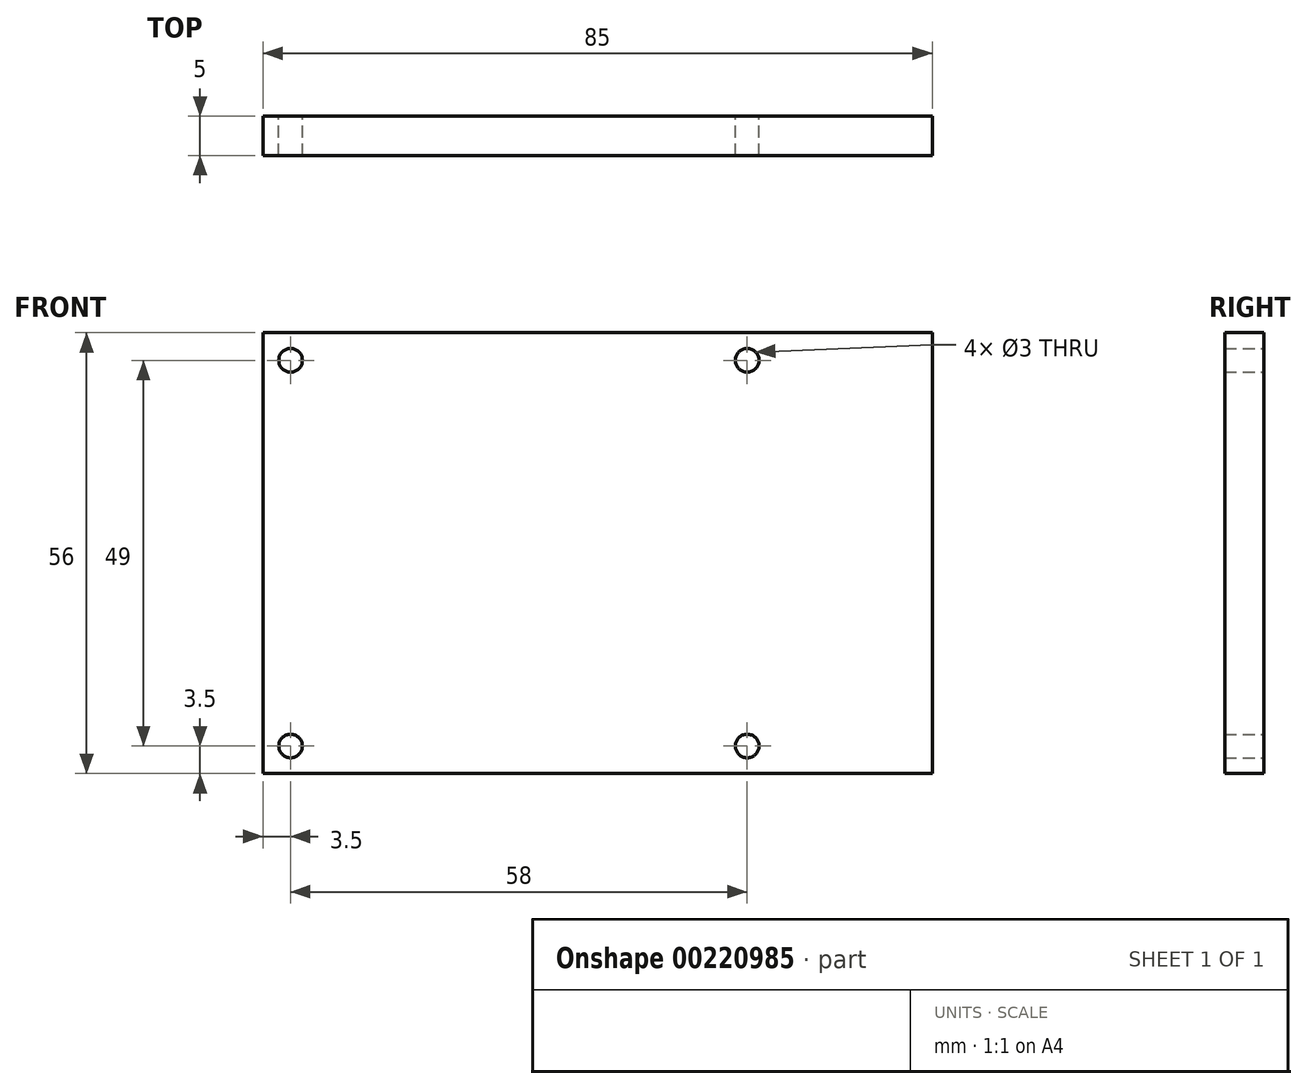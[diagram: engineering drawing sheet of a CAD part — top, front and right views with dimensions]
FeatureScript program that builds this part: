
annotation { "Feature Type Name" : "Feature", "Feature Type Description" : "" }
export const myFeature = defineFeature(function(context is Context, id is Id, definition is map)
    precondition{}
    {
        {
            var Q0;
            Q0=qCreatedBy(makeId("Front.planeOp"),FACE);
            var sketch = newSketch(context, id + "F0", { "sketchPlane" : qUnion([Q0])});
            skLineSegment(sketch, "E0.bottom", {"start": v(42.5, 28) * mm, "end": v(-42.5, 28) * mm});
            skLineSegment(sketch, "E0.top", {"start": v(42.5, -28) * mm, "end": v(-42.5, -28) * mm});
            skLineSegment(sketch, "E0.left", {"start": v(42.5, 28) * mm, "end": v(42.5, -28) * mm});
            skLineSegment(sketch, "E0.right", {"start": v(-42.5, 28) * mm, "end": v(-42.5, -28) * mm});
            skPoint(sketch, "E0.middle", {"position": v(0, 0) * mm});
            skLineSegment(sketch, "E1", {"start": v(-42.5, -28) * mm, "end": v(-39, -28) * mm});
            skLineSegment(sketch, "E2", {"start": v(-39, -28) * mm, "end": v(-39, -24.5) * mm});
            skLineSegment(sketch, "E3", {"start": v(-42.5, 28) * mm, "end": v(-39, 28) * mm});
            skLineSegment(sketch, "E4", {"start": v(-39, 28) * mm, "end": v(-39, 24.5) * mm});
            skCircle(sketch, "E5", {"center": v(-39, 24.5) * mm, "radius": 1.5 * mm});
            skCircle(sketch, "E6", {"center": v(-39, -24.5) * mm, "radius": 1.5 * mm});
            skLineSegment(sketch, "E7", {"start": v(-39, 24.5) * mm, "end": v(19, 24.5) * mm});
            skCircle(sketch, "E8", {"center": v(19, 24.5) * mm, "radius": 1.5 * mm});
            skLineSegment(sketch, "E9", {"start": v(-39, -24.5) * mm, "end": v(19, -24.5) * mm});
            skCircle(sketch, "E10", {"center": v(19, -24.5) * mm, "radius": 1.5 * mm});
            skLineSegment(sketch, "E11", {"start": v(19, 24.5) * mm, "end": v(42.5, 24.5) * mm});
            skSolve(sketch);
        }
        {
            var Q0;
            Q0 = qSketchRegion(id + "F0", true);
            extrude(context, id + "F1", {"entities" : qUnion([Q0]), "offsetDistance" : 25 * mm, "depth" : 5 * mm});
        }
    });
